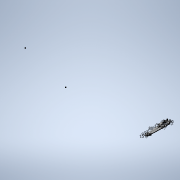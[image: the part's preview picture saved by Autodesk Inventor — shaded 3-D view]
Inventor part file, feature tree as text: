
AUTODESK INVENTOR PART (.ipt)
format: ipt  version: 2020.3 (Build 243373000, 373)  size: 203,264 bytes
history: native  units: mm
features: fillet x4, hole x2, sketch x1, extrude x1, chamfer x1
ambient origin geometry x8: Origin, YZ Plane, XZ Plane, XY Plane, X Axis, Y Axis, Z Axis, Center Point
bodies: Solid1 (feature_tree)
feature tree (9):
  sketch  "Sketch1"  dims[d4=5.0mm d5=23.0mm d6=13.0mm d7=5.0mm d15=7.0mm d17=5.0mm d18=4.0mm d21=20.0mm d23=80.0mm d24=15.0mm d29=29.670597mm d30=6.0mm d31=10.0mm d33=5.0mm d34=0.0mm d37=2.5mm d38=2.0mm d39=45.0deg d40=3.0mm d41=3.0mm d42=2.0mm d43=4.0mm d44=3.0mm d45=4.0mm d50=13.0mm d51=12.0mm d52=22.68928mm d53=16.057029mm d54=2.0mm d55=6.0mm d56=4.0mm d57=2.0mm d58=90.0deg d59=8.0mm d60=20.594885mm d61=0.5mm d62=2.0mm d63=4.0mm d64=4.0mm d65=2.0mm d66=90.0deg d67=8.0mm d68=20.594885mm]
  extrude  "Extrusion1"  Depth=23.0mm
  chamfer  "Chamfer1"  Distance=13.0mm
  fillet  "Fillet1"  Radius=5.0mm
  fillet  "Fillet2"  Radius=7.0mm
  fillet  "Fillet3"  Radius=5.0mm
  hole  "Hole1"  [1 undecoded]
  fillet  "Fillet4"  Radius=20.0mm
  hole  "Hole2"  [1 undecoded]
note: 2 required parameter values undecoded (feature->parameter linkage not recoverable at this tier; creation-order binding heuristic only, values carry confidence <= 0.55)
